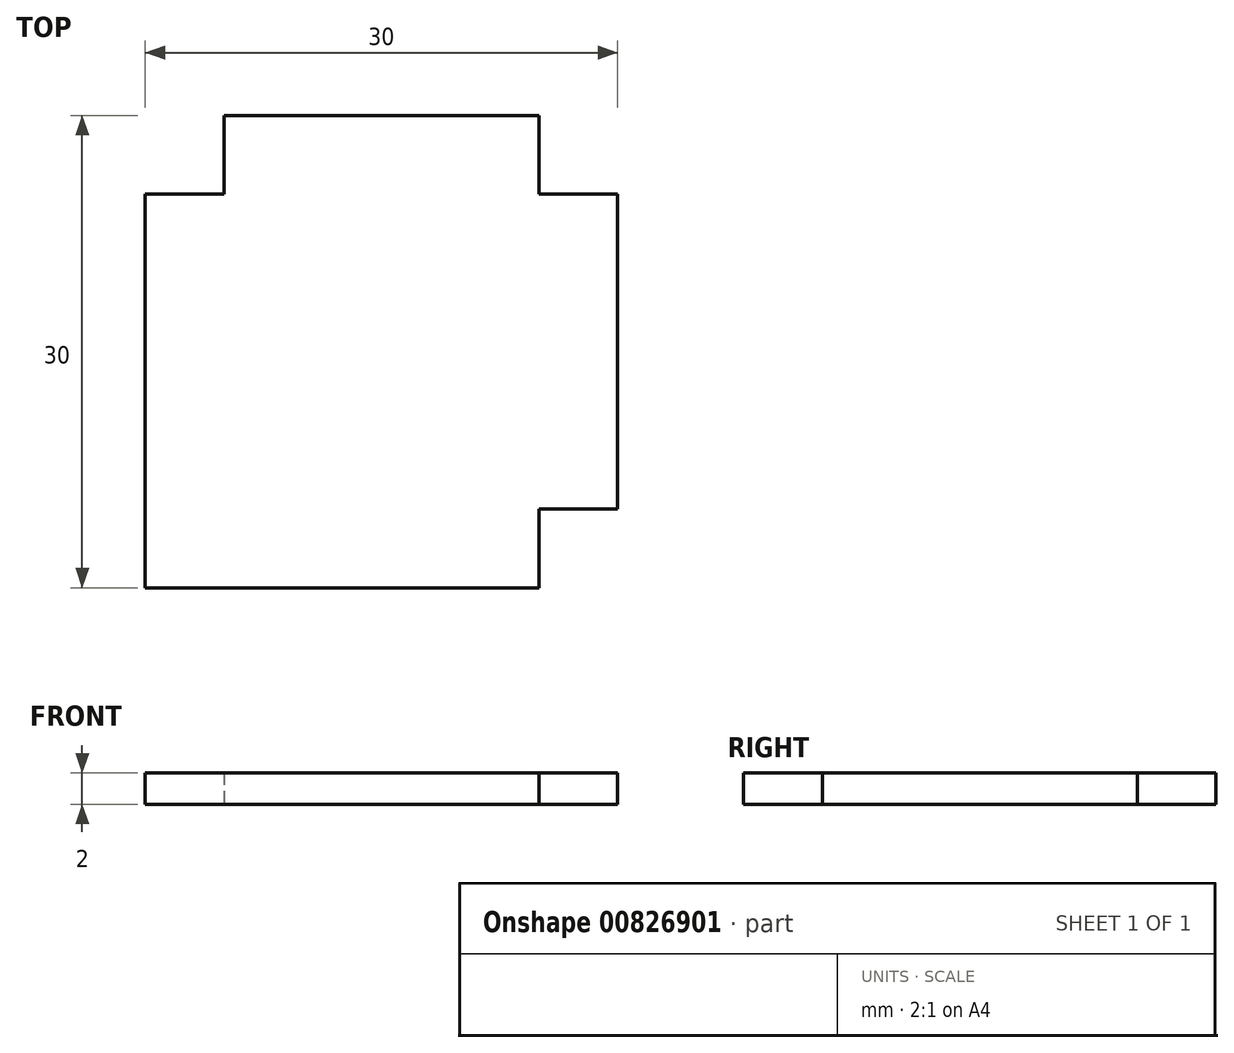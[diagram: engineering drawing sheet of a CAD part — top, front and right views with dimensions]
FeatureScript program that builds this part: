
annotation { "Feature Type Name" : "Feature", "Feature Type Description" : "" }
export const myFeature = defineFeature(function(context is Context, id is Id, definition is map)
    precondition{}
    {
        {
            var Q0;
            Q0=qCreatedBy(makeId("Top.planeOp"),FACE);
            var sketch = newSketch(context, id + "F0", { "sketchPlane" : qUnion([Q0])});
            skLineSegment(sketch, "E0.bottom", {"start": v(15, -15) * mm, "end": v(-15, -15) * mm});
            skLineSegment(sketch, "E0.top", {"start": v(15, 15) * mm, "end": v(-15, 15) * mm});
            skLineSegment(sketch, "E0.left", {"start": v(15, -15) * mm, "end": v(15, 15) * mm});
            skLineSegment(sketch, "E0.right", {"start": v(-15, -10) * mm, "end": v(-15, 15) * mm});
            skPoint(sketch, "E0.middle", {"position": v(0, 0) * mm});
            skLineSegment(sketch, "E1.bottom", {"start": v(15, 15) * mm, "end": v(10, 15) * mm});
            skLineSegment(sketch, "E1.top", {"start": v(15, 10) * mm, "end": v(10, 10) * mm});
            skLineSegment(sketch, "E1.left", {"start": v(15, 15) * mm, "end": v(15, 10) * mm});
            skLineSegment(sketch, "E1.right", {"start": v(10, 15) * mm, "end": v(10, 10) * mm});
            skLineSegment(sketch, "E2.bottom", {"start": v(-15, 15) * mm, "end": v(-10, 15) * mm});
            skLineSegment(sketch, "E2.top", {"start": v(-15, 10) * mm, "end": v(-10, 10) * mm});
            skLineSegment(sketch, "E2.left", {"start": v(-15, 15) * mm, "end": v(-15, 10) * mm});
            skLineSegment(sketch, "E2.right", {"start": v(-10, 15) * mm, "end": v(-10, 10) * mm});
            skLineSegment(sketch, "E3.bottom", {"start": v(-15, -15) * mm, "end": v(-10, -15) * mm});
            skLineSegment(sketch, "E3.left", {"start": v(-15, -15) * mm, "end": v(-15, -10) * mm});
            skLineSegment(sketch, "E3.right", {"start": v(-10, -15) * mm, "end": v(-10, -10) * mm});
            skLineSegment(sketch, "E4.bottom", {"start": v(15, -15) * mm, "end": v(10, -15) * mm});
            skLineSegment(sketch, "E4.top", {"start": v(15, -10) * mm, "end": v(10, -10) * mm});
            skLineSegment(sketch, "E4.left", {"start": v(15, -15) * mm, "end": v(15, -10) * mm});
            skLineSegment(sketch, "E4.right", {"start": v(10, -15) * mm, "end": v(10, -10) * mm});
            skSolve(sketch);
        }
        {
            var Q0;
            Q0=makeQuery(id+"F0.imprint","IMPRINT",FACE,{"disambiguationData":[TD([[makeQuery(id+"F0.imprint","IMPRINT",EDGE,{"derivedFrom":sQuery(id+"F0.wireOp",EDGE,"E0.bottom")}),-1.0]])]});
            extrude(context, id + "F1", {"entities" : qUnion([Q0]), "depth" : 2 * mm, "offsetDistance" : 25 * mm});
        }
    });
